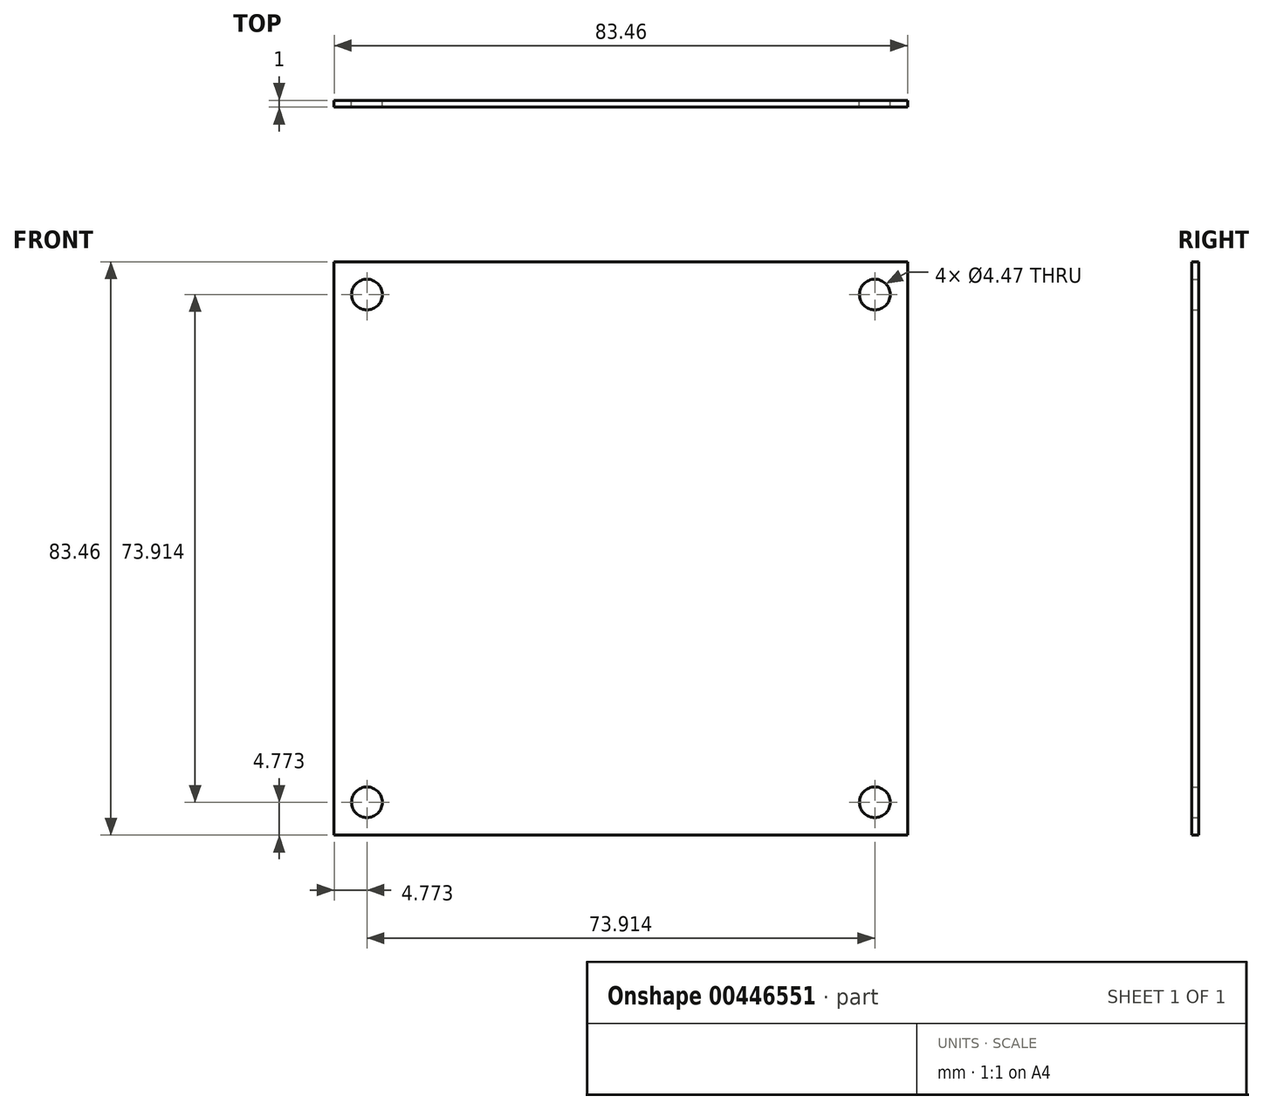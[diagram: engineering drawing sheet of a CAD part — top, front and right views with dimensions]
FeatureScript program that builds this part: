
annotation { "Feature Type Name" : "Feature", "Feature Type Description" : "" }
export const myFeature = defineFeature(function(context is Context, id is Id, definition is map)
    precondition{}
    {
        {
            var Q0;
            Q0=qCreatedBy(makeId("Front.planeOp"),FACE);
            var sketch = newSketch(context, id + "F0", { "sketchPlane" : qUnion([Q0])});
            skCircle(sketch, "E0", {"center": v(0, 0) * mm, "radius": 36.96 * mm, "construction": true});
            skLineSegment(sketch, "E1.bottom", {"start": v(-36.96, 36.96) * mm, "end": v(36.96, 36.96) * mm, "construction": true});
            skLineSegment(sketch, "E1.top", {"start": v(-36.96, -36.96) * mm, "end": v(36.96, -36.96) * mm, "construction": true});
            skLineSegment(sketch, "E1.left", {"start": v(-36.96, 36.96) * mm, "end": v(-36.96, -36.96) * mm, "construction": true});
            skLineSegment(sketch, "E1.right", {"start": v(36.96, 36.96) * mm, "end": v(36.96, -36.96) * mm, "construction": true});
            skCircle(sketch, "E2", {"center": v(36.96, -36.96) * mm, "radius": 2.24 * mm});
            skCircle(sketch, "E3", {"center": v(36.96, 36.96) * mm, "radius": 2.24 * mm});
            skCircle(sketch, "E4", {"center": v(-36.96, 36.96) * mm, "radius": 2.24 * mm});
            skCircle(sketch, "E5", {"center": v(-36.96, -36.96) * mm, "radius": 2.24 * mm});
            skLineSegment(sketch, "E6.bottom", {"start": v(41.73, -41.73) * mm, "end": v(-41.73, -41.73) * mm});
            skLineSegment(sketch, "E6.top", {"start": v(41.73, 41.73) * mm, "end": v(-41.73, 41.73) * mm});
            skLineSegment(sketch, "E6.left", {"start": v(41.73, -41.73) * mm, "end": v(41.73, 41.73) * mm});
            skLineSegment(sketch, "E6.right", {"start": v(-41.73, -41.73) * mm, "end": v(-41.73, 41.73) * mm});
            skSolve(sketch);
        }
        {
            var Q0;
            Q0=qSketchRegion(id+"F0",true);
            extrude(context, id + "F1", {"entities" : qUnion([Q0]), "depth" : 1 * mm});
        }
    });
